# Revit family: Basin-Wall_Hung-Sloan-(SS-3004_SS-3104_SS-3804)_Series
name_source: partatom
category: Plumbing Fixtures
revit_build: Autodesk Revit 2014 (Build: 20130308_1515(x64)
units: mm (PartAtom-declared; Revit-internal decimal feet)

## types (3) — shared parameters
ADA Compliant = Yes
Assembly Code = D2010440
Cold Water Connection Diameter = 3/8"
Default Elevation = 34"
Fixture Color = White
Hot Water Connection Diameter = 3/8"
IAPMO Certification = cUPC
Manufacturer = Sloan
Material = Vitreous China-Sloan-White
Mounting = Wall Hung
Price = Prices may vary. Please consult Sloan Rep for most up-to-date price list.
Product Documentation Link = https://specifications.sloan.com
Product URL = https://www.sloan.com
URL = http://www.sloan.com
Vent Connection = No
Warranty Information = 3 Year (Limited)
Waste Connection = Yes
Waste Connection Diameter = 1 1/4"

## per-type parameters (varying)
| type | CW Connection | CWFU | Description | HW Connection | HWFU | Hole Punch Location | Hole Visibility | Order Code | WFU |
| SS-3804 | Yes | 1.5 | Complete ADA wall hung vitreous china lavatory, with 8" centers. | Yes | 1.5 | 8" | Yes | 3873804 | 2 |
| SS-3004 | Yes | 1.5 | Complete ADA wall hung vitreous china lavatory, with 4" centers. | Yes | 1.5 | 4" | Yes | 3873004 | 2 |
| SS-3104 | No | 0 | Complete ADA wall hung vitreous china lavatory, with single hole. | No | 0 | 30" | No | 3873104 | 0 |

note: column(s) folded — value = type name in every type: Model

## geometry (parser evidence)
native form markers: Sweep x1
no freeform markers — native parametric forms only
